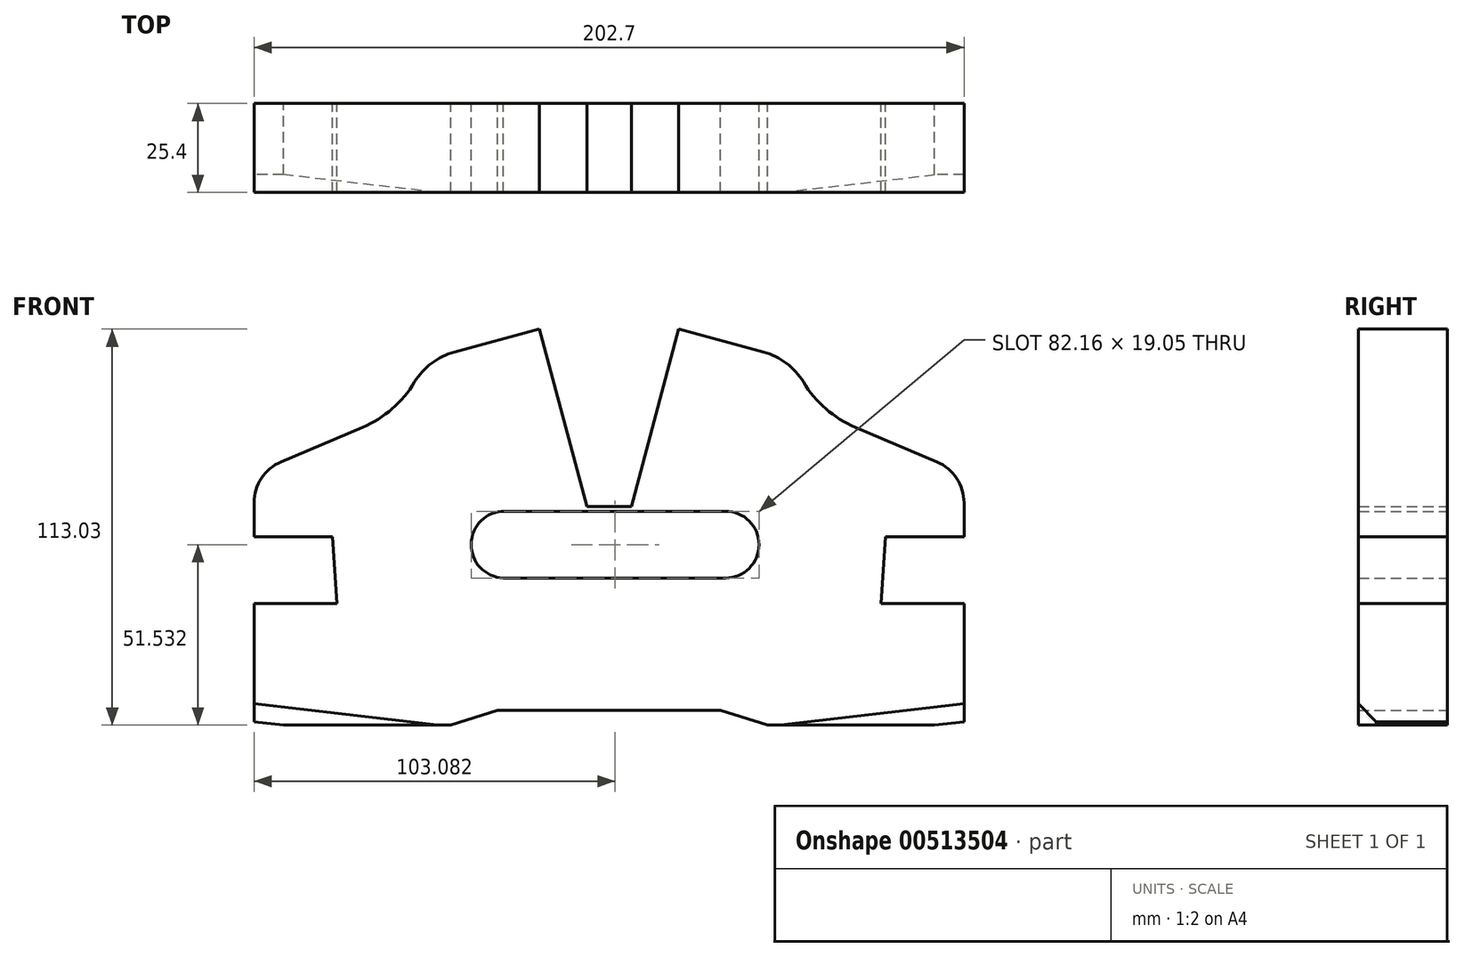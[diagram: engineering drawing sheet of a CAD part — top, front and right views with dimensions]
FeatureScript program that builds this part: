
annotation { "Feature Type Name" : "Feature", "Feature Type Description" : "" }
export const myFeature = defineFeature(function(context is Context, id is Id, definition is map)
    precondition{}
    {
        {
            var Q0;
            Q0=qCreatedBy(makeId("Front.planeOp"),FACE);
            var sketch = newSketch(context, id + "F0", { "sketchPlane" : qUnion([Q0])});
            skLineSegment(sketch, "E0", {"start": v(0, 77.73) * mm, "end": v(0, -47.05) * mm, "construction": true});
            skLineSegment(sketch, "E1", {"start": v(-77.65, 5.1) * mm, "end": v(-101.35, 5.1) * mm});
            skLineSegment(sketch, "E2", {"start": v(-92.9, -29.66) * mm, "end": v(-45.21, -29.66) * mm});
            skLineSegment(sketch, "E3", {"start": v(-45.21, -29.66) * mm, "end": v(-31.83, -25.38) * mm});
            skLineSegment(sketch, "E4.MirrorCS", {"start": v(45.21, -29.66) * mm, "end": v(31.83, -25.38) * mm});
            skLineSegment(sketch, "E5", {"start": v(-31.83, -25.38) * mm, "end": v(31.83, -25.38) * mm});
            skLineSegment(sketch, "E6", {"start": v(-78.87, 24.15) * mm, "end": v(-77.65, 5.1) * mm});
            skLineSegment(sketch, "E7", {"start": v(-101.35, 5.1) * mm, "end": v(-101.35, -28.68) * mm});
            skLineSegment(sketch, "E8", {"start": v(-101.35, -28.68) * mm, "end": v(-92.9, -29.66) * mm});
            skLineSegment(sketch, "E9", {"start": v(-30.21, 12.35) * mm, "end": v(33.29, 12.35) * mm});
            skLineSegment(sketch, "E10", {"start": v(-29.82, 31.4) * mm, "end": v(33.29, 31.4) * mm});
            skArc(sketch, "E11", {"start": v(-29.82, 31.4) * mm, "mid": v(-39.35, 22.07) * mm, "end": v(-30.21, 12.35) * mm});
            skArc(sketch, "E12", {"start": v(33.29, 12.35) * mm, "mid": v(42.81, 21.87) * mm, "end": v(33.29, 31.4) * mm});
            skLineSegment(sketch, "E13", {"start": v(-78.87, 24.15) * mm, "end": v(-101.35, 24.15) * mm});
            skLineSegment(sketch, "E14", {"start": v(-101.35, 24.15) * mm, "end": v(-101.35, 33.8) * mm});
            skArc(sketch, "E15", {"start": v(-101.35, 33.8) * mm, "mid": v(-99.24, 40.81) * mm, "end": v(-93.61, 45.5) * mm});
            skLineSegment(sketch, "E16", {"start": v(-93.61, 45.5) * mm, "end": v(-70.3, 55.4) * mm});
            skArc(sketch, "E17", {"start": v(-70.3, 55.4) * mm, "mid": v(-61.88, 60.66) * mm, "end": v(-55.5, 68.28) * mm});
            skArc(sketch, "E18", {"start": v(-55.5, 68.28) * mm, "mid": v(-50.64, 73.69) * mm, "end": v(-44.1, 76.88) * mm});
            skLineSegment(sketch, "E19", {"start": v(-44.1, 76.88) * mm, "end": v(-19.9, 83.37) * mm});
            skLineSegment(sketch, "E20", {"start": v(-6.35, 32.77) * mm, "end": v(-19.9, 83.37) * mm});
            skLineSegment(sketch, "E21", {"start": v(-6.35, 32.77) * mm, "end": v(18.86, 32.77) * mm});
            skLineSegment(sketch, "E22.MirrorCS", {"start": v(6.35, 32.77) * mm, "end": v(19.9, 83.37) * mm});
            skLineSegment(sketch, "E23.MirrorCS", {"start": v(44.1, 76.88) * mm, "end": v(19.9, 83.37) * mm});
            skArc(sketch, "E24.MirrorCS", {"start": v(55.5, 68.28) * mm, "mid": v(50.64, 73.69) * mm, "end": v(44.1, 76.88) * mm});
            skArc(sketch, "E25.MirrorCS", {"start": v(70.3, 55.4) * mm, "mid": v(61.88, 60.66) * mm, "end": v(55.5, 68.28) * mm});
            skLineSegment(sketch, "E26.MirrorCS", {"start": v(93.61, 45.5) * mm, "end": v(70.3, 55.4) * mm});
            skArc(sketch, "E27.MirrorCS", {"start": v(101.35, 33.8) * mm, "mid": v(99.24, 40.81) * mm, "end": v(93.61, 45.5) * mm});
            skLineSegment(sketch, "E28.MirrorCS", {"start": v(101.35, 24.15) * mm, "end": v(101.35, 33.8) * mm});
            skLineSegment(sketch, "E29.MirrorCS", {"start": v(78.87, 24.15) * mm, "end": v(101.35, 24.15) * mm});
            skLineSegment(sketch, "E30.MirrorCS", {"start": v(78.87, 24.15) * mm, "end": v(77.65, 5.1) * mm});
            skLineSegment(sketch, "E31.MirrorCS", {"start": v(77.65, 5.1) * mm, "end": v(101.35, 5.1) * mm});
            skLineSegment(sketch, "E32.MirrorCS", {"start": v(101.35, 5.1) * mm, "end": v(101.35, -28.68) * mm});
            skLineSegment(sketch, "E33.MirrorCS", {"start": v(101.35, -28.68) * mm, "end": v(92.9, -29.66) * mm});
            skLineSegment(sketch, "E34.MirrorCS", {"start": v(92.9, -29.66) * mm, "end": v(45.21, -29.66) * mm});
            skSolve(sketch);
        }
        {
            var Q0;
            Q0 = qSketchRegion(id + "F0", true);
            extrude(context, id + "F1", {"entities" : qUnion([Q0]), "endBound" : BoundingType.SYMMETRIC, "depth" : 25.4 * mm, "offsetDistance" : 25.4 * mm});
        }
        {
            var Q0;
            Q0=makeQuery(id+"F1.opExtrude","CAP_EDGE",EDGE,{"disambiguationData":[OSD([sQuery(id+"F0.wireOp",EDGE,"E8")])],"isStart":false});
            var Q1;
            Q1=makeQuery(id+"F1.opExtrude","CAP_EDGE",EDGE,{"disambiguationData":[OSD([sQuery(id+"F0.wireOp",EDGE,"E33.MirrorCS")])],"isStart":false});
            chamfer(context, id + "F2", {"entities" : qUnion([Q0, Q1]), "width" : 5.08 * mm, "tangentPropagation" : true});
        }
    });
